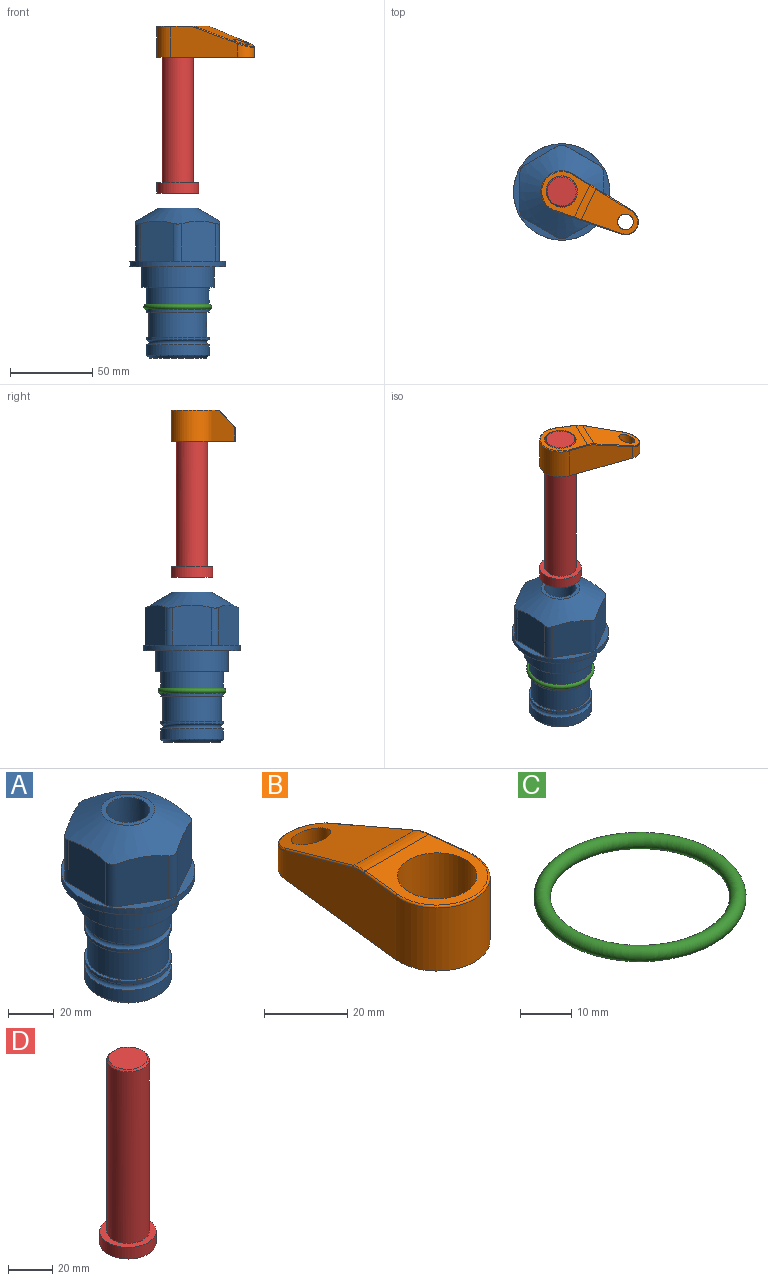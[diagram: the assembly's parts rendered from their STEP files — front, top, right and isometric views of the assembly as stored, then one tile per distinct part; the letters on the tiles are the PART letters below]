
ASSEMBLY  parts=4 mates=2
PART A: 36 faces, bbox 58.7x58.7x91.2 mm
  f0: cylinder r=17.78mm len=35.56mm, axis (0,0,1), area 1670.8mm2, adj f23,f24,f31
  f1: cylinder r=19.05mm len=38.1mm, axis (0,0,1), area 1191.9mm2, adj f26,f27,f30
  f2: plane 58.66x58.66mm, normal (0,0,-1), area 1150.6mm2, adj f3,f28
  f3: cylinder r=29.33mm len=58.66mm, axis (0,0,-1), area 585.1mm2, adj f2,f4
  f4: plane 58.66x58.66mm, normal (0,0,1), area 475.9mm2, adj f3,f5,f6,f7,f8,f9,f10,f11
  f5: plane 24.5x20.32mm, normal (-0.5,0.87,0), area 562.8mm2, adj f4,f15,f16,f17
  f6: plane 24.5x20.32mm, normal (0.5,0.87,0), area 562.8mm2, adj f4,f14,f15,f17
  f7: plane 24.5x23.48mm, normal (1,0,0), area 562.8mm2, adj f4,f13,f14,f17
  f8: plane 24.5x20.32mm, normal (0.5,-0.87,0), area 562.8mm2, adj f4,f12,f13,f17
  f9: plane 24.5x20.32mm, normal (-0.5,-0.87,0), area 562.8mm2, adj f4,f11,f12,f17
  f10: plane 24.5x23.48mm, normal (-1,0,0), area 562.8mm2, adj f4,f11,f16,f17
  f11: cylinder r=5.08mm len=23.01mm, axis (0,0,-1), area 121.2mm2, adj f4,f9,f10,f17
  f12: cylinder r=5.08mm len=23.01mm, axis (0,0,-1), area 121.2mm2, adj f4,f8,f9,f17
  f13: cylinder r=5.08mm len=23.01mm, axis (0,0,-1), area 121.2mm2, adj f4,f7,f8,f17
  f14: cylinder r=5.08mm len=23.01mm, axis (0,0,-1), area 121.2mm2, adj f4,f6,f7,f17
  f15: cylinder r=5.08mm len=23.01mm, axis (0,0,-1), area 121.2mm2, adj f4,f5,f6,f17
  f16: cylinder r=5.08mm len=23.01mm, axis (0,0,-1), area 121.2mm2, adj f4,f5,f10,f17
  f17: cone r=11.73mm half-angle=60deg, axis (0,0,-1), area 2071.8mm2, adj f5,f6,f7,f8,f9,f10,f11,f12
  f18: plane 23.46x23.46mm, normal (0,0,1), area 147.4mm2, adj f17,f35
  f19: plane 34.93x34.93mm, normal (0,0,-1), area 958mm2, adj f29
  f20: cylinder r=19.05mm len=38.1mm, axis (0,0,1), area 760.1mm2, adj f21,f29
  f21: torus R=19.05mm, axis (0,0,1), area 565.3mm2, adj f20,f22
  f22: cylinder r=19.05mm len=38.1mm, axis (0,0,1), area 190mm2, adj f21,f23
  f23: plane 38.1x38.1mm, normal (0,0,1), area 146.9mm2, adj f0,f22
  f24: plane 38.1x38.1mm, normal (0,0,-1), area 146.9mm2, adj f0,f25
  f25: cylinder r=19.05mm len=38.1mm, axis (0,0,1), area 190mm2, adj f24,f26
  f26: torus R=19.05mm, axis (0,0,1), area 565.3mm2, adj f1,f25
  f27: plane 44.45x44.45mm, normal (0,0,-1), area 411.7mm2, adj f1,f28
  f28: cylinder r=22.23mm len=44.45mm, axis (0,0,1), area 1773.5mm2, adj f2,f27
  f29: cone r=19.05mm half-angle=45deg, axis (0,0,1), area 257.5mm2, adj f19,f20
  f30: cylinder r=3.17mm len=6.75mm, axis (-1,0,0), area 128mm2, adj f1,f33
  f31: cylinder r=3.17mm len=6.35mm, axis (-1,0,0), area 102.5mm2, adj f0,f33
  f32: plane 25.4x25.4mm, normal (0,0,1), area 506.7mm2, adj f33
  f33: cylinder r=12.7mm len=66.42mm, axis (0,0,-1), area 5236.2mm2, adj f30,f31,f32,f34
  f34: cone r=9.53mm half-angle=30deg, axis (0,0,-1), area 443.4mm2, adj f33,f35
  f35: cylinder r=9.53mm len=19.05mm, axis (0,0,-1), area 849mm2, adj f18,f34
PART B: 44 faces, bbox 27.5x64.5x19.1 mm
  f0: plane 2.3x0.95mm, normal (0,0,-1), area 1mm2, adj f25,f30,f34
  f1: plane 63.5x25.4mm, normal (0,0,-1), area 561.7mm2, adj f2,f3,f4,f5,f6,f7,f19,f20
  f2: cylinder r=12.7mm len=25.4mm, axis (0,0,-1), area 792.2mm2, adj f1,f3,f5,f13
  f3: plane 42.33x18.54mm, normal (0.99,0.11,0), area 647mm2, adj f1,f2,f4,f11,f12,f14
  f4: cylinder r=7.94mm len=15.78mm, axis (0,0,-1), area 158.6mm2, adj f1,f3,f5,f16
  f5: plane 42.33x18.54mm, normal (-0.99,0.11,0), area 647mm2, adj f1,f2,f4,f15,f17,f18
  f6: cylinder r=9.53mm len=19.05mm, axis (0,0,-1), area 1140.1mm2, adj f1,f8
  f7: cylinder r=4.76mm len=10.98mm, axis (0,0,-1), area 276.1mm2, adj f1,f9
  f8: plane 25.83x24.38mm, normal (0,0,1), area 262.2mm2, adj f6,f10,f11,f13,f15
  f9: plane 32.49x20.55mm, normal (0,0.34,0.94), area 489.9mm2, adj f7,f10,f14,f16,f18
  f10: cylinder r=12.7mm len=21.49mm, axis (-1,0,0), area 93.2mm2, adj f8,f9,f12,f17
  f11: cylinder r=0.51mm len=12.34mm, axis (0.11,-0.99,0), area 9.9mm2, adj f3,f8,f12,f13
  f12: bspline ~7.62x1.64mm, area 3.5mm2, adj f3,f10,f11,f14
  f13: torus R=12.19mm, axis (0,0,1), area 33.6mm2, adj f2,f8,f11,f15
  f14: cylinder r=0.51mm len=26.01mm, axis (0.1,-0.93,0.34), area 21.6mm2, adj f3,f9,f12,f16
  f15: cylinder r=0.51mm len=12.34mm, axis (0.11,0.99,0), area 9.9mm2, adj f5,f8,f13,f17
  f16: bspline ~15.78x7.05mm, area 15.7mm2, adj f4,f9,f14,f18
  f17: bspline ~7.62x1.64mm, area 3.5mm2, adj f5,f10,f15,f18
  f18: cylinder r=0.51mm len=26.01mm, axis (0.1,0.93,-0.34), area 21.6mm2, adj f5,f9,f16,f17
  f19: plane 21.6x14.29mm, normal (-0.99,-0.11,0), area 242.6mm2, adj f1,f26,f28,f34,f36,f38
  f20: plane 21.6x14.29mm, normal (0.99,-0.11,0), area 242.6mm2, adj f1,f27,f29,f37,f39,f41
  f21: cylinder r=12.7mm len=14.29mm, axis (0,0,-1), area 173.2mm2, adj f1,f26,f27,f30,f31,f33
  f22: cylinder r=7.94mm len=7.63mm, axis (0,0,-1), area 53.8mm2, adj f1,f28,f29,f42
  f23: plane 2.3x0.95mm, normal (0,0,-1), area 1mm2, adj f25,f33,f37
  f24: plane 17.94x12.32mm, normal (0,-0.34,-0.94), area 191.2mm2, adj f25,f38,f41,f42
  f25: cylinder r=9.53mm len=12.93mm, axis (-1,0,0), area 37.5mm2, adj f0,f23,f24,f31,f36,f39
  f26: cylinder r=1.59mm len=14.29mm, axis (0,0,-1), area 49mm2, adj f1,f19,f21,f32
  f27: cylinder r=1.59mm len=14.29mm, axis (0,0,-1), area 49mm2, adj f1,f20,f21,f35
  f28: cylinder r=1.59mm len=7.28mm, axis (0,0,-1), area 22.1mm2, adj f1,f19,f22,f40
  f29: cylinder r=1.59mm len=7.28mm, axis (0,0,-1), area 22.1mm2, adj f1,f20,f22,f43
  f30: torus R=14.29mm, axis (0,0,1), area 5.8mm2, adj f0,f21,f31,f32
  f31: bspline ~11.06x2.73mm, area 20.8mm2, adj f21,f25,f30,f33
  f32: sphere r=1.59mm, area 5.4mm2, adj f26,f30,f34
  f33: torus R=14.29mm, axis (0,0,1), area 5.8mm2, adj f21,f23,f31,f35
  f34: cylinder r=1.59mm len=1.68mm, axis (-0.11,0.99,0), area 2.4mm2, adj f0,f19,f32,f36
  f35: sphere r=1.59mm, area 5.4mm2, adj f27,f33,f37
  f36: bspline ~5.82x2.33mm, area 7.7mm2, adj f19,f25,f34,f38
  f37: cylinder r=1.59mm len=1.68mm, axis (0.11,0.99,0), area 2.4mm2, adj f20,f23,f35,f39
  f38: cylinder r=1.59mm len=18.33mm, axis (0.1,-0.93,0.34), area 46.7mm2, adj f19,f24,f36,f40
  f39: bspline ~5.82x2.33mm, area 7.7mm2, adj f20,f25,f37,f41
  f40: sphere r=1.59mm, area 3.6mm2, adj f28,f38,f42
  f41: cylinder r=1.59mm len=18.33mm, axis (0.1,0.93,-0.34), area 46.7mm2, adj f20,f24,f39,f43
  f42: bspline ~8.31x1.84mm, area 15.3mm2, adj f22,f24,f40,f43
  f43: sphere r=1.59mm, area 3.6mm2, adj f29,f41,f42
PART C: 1 faces, bbox 44.7x44.7x3.2 mm
  f0: torus R=19.05mm, axis (0,0,1), area 1193.9mm2
PART D: 6 faces, bbox 25.4x25.4x101.6 mm
  f0: plane 17.46x17.46mm, normal (0,0,1), area 239.5mm2, adj f5
  f1: plane 25.4x25.4mm, normal (0,0,-1), area 506.7mm2, adj f2
  f2: cylinder r=12.7mm len=25.4mm, axis (0,0,1), area 506.7mm2, adj f1,f3
  f3: plane 25.4x25.4mm, normal (0,0,1), area 221.7mm2, adj f2,f4
  f4: cylinder r=9.53mm len=94.46mm, axis (0,0,1), area 5653mm2, adj f3,f5
  f5: cone r=8.73mm half-angle=45deg, axis (0,0,-1), area 64.4mm2, adj f0,f4
PLACE A at identity fixed
PLACE B rot(axis=(0,0,-1),115.4deg) t=(0,0,127.26)mm
PLACE C at identity
PLACE D rot(axis=(0,0,-1),115.4deg) t=(0,0,72.65)mm
MATE fastened B.f2 <-> D.f2  axis (0,0,1) through (0,0,146.31)mm
MATE cylindrical D.f2 <-> A.f0  axis (0,0,1) through (0,0,98.29)mm
